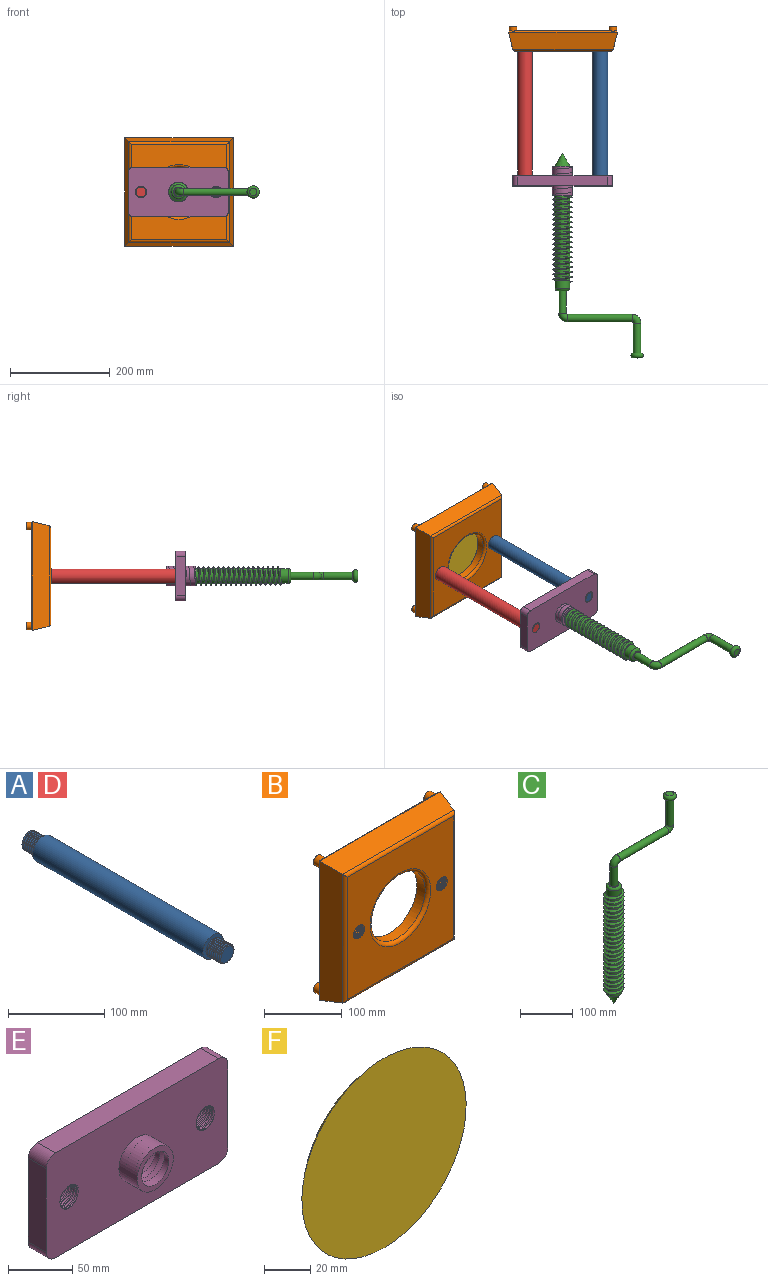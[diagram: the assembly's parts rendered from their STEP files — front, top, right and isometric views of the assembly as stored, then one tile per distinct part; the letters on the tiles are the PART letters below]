
ASSEMBLY  parts=6 mates=5
PART A: 17 faces, bbox 30x293x30 mm
  f0: cylinder r=15mm len=250mm, axis (0,1,0), area 23561.9mm2, adj f1,f2
  f1: plane 30x30mm, normal (0,-1,0), area 392.7mm2, adj f0,f3
  f2: plane 30x30mm, normal (0,1,0), area 392.7mm2, adj f0,f5
  f3: cylinder r=10mm len=20mm, axis (0,1,0), area 531.6mm2, adj f1,f4,f13,f15,f16
  f4: plane 20x20mm, normal (0,-1,0), area 314.2mm2, adj f3,f12
  f5: cylinder r=10mm len=20mm, axis (0,-1,0), area 531.6mm2, adj f2,f6,f8,f10,f11
  f6: plane 20x20mm, normal (0,1,0), area 314.2mm2, adj f5,f7
  f7: cylinder r=10mm len=20mm, axis (0,1,0), area 24.7mm2, adj f6,f9,f10
  f8: plane 1.5x1.3mm, normal (0,0,1), area 1mm2, adj f5,f10,f11
  f9: plane 1.5x1.3mm, normal (0,0,-1), area 1mm2, adj f7,f10,f11
  f10: bspline ~26.09x22.6mm, area 702.4mm2, adj f5,f7,f8,f9,f11
  f11: bspline ~26.09x22.6mm, area 702.4mm2, adj f5,f8,f9,f10
  f12: cylinder r=10mm len=20mm, axis (0,-1,0), area 24.7mm2, adj f4,f14,f15
  f13: plane 1.5x1.3mm, normal (0,0,1), area 1mm2, adj f3,f15,f16
  f14: plane 1.5x1.3mm, normal (0,0,-1), area 1mm2, adj f12,f15,f16
  f15: bspline ~26.09x22.6mm, area 702.4mm2, adj f3,f12,f13,f14,f16
  f16: bspline ~26.09x22.6mm, area 702.4mm2, adj f3,f13,f14,f15
PART B: 45 faces, bbox 219.1x50.6x219.1 mm
  f0: cylinder r=10mm len=20mm, axis (0,-1,0), area 531.6mm2, adj f7,f16,f42,f43,f44
  f1: cylinder r=10mm len=20mm, axis (0,-1,0), area 531.6mm2, adj f7,f16,f39,f40,f41
  f2: plane 214x214mm, normal (0,1,0), area 10968.7mm2, adj f18,f20,f22,f24,f31,f32,f33,f34
  f3: plane 4.31x4.31mm, normal (0,1,0), area 6.6mm2, adj f24,f37,f38
  f4: plane 4.31x4.31mm, normal (0,1,0), area 6.6mm2, adj f22,f36,f38
  f5: plane 4.31x4.31mm, normal (0,1,0), area 6.6mm2, adj f20,f35,f37
  f6: plane 4.31x4.31mm, normal (0,1,0), area 6.6mm2, adj f18,f35,f36
  f7: plane 192.19x192.19mm, normal (0,-1,0), area 26806.2mm2, adj f0,f1,f26,f27,f28,f29,f30
  f8: plane 218.54x33.3mm, normal (0,-0.24,-0.97), area 7216.2mm2, adj f9,f11,f29,f38
  f9: plane 218.54x33.3mm, normal (-0.97,-0.24,0), area 7216.2mm2, adj f8,f10,f27,f37
  f10: plane 218.54x33.3mm, normal (0,-0.24,0.97), area 7216.2mm2, adj f9,f11,f28,f35
  f11: plane 218.54x33.3mm, normal (0.97,-0.24,0), area 7216.2mm2, adj f8,f10,f30,f36
  f12: plane 180x17.66mm, normal (0,0,-1), area 3178.4mm2, adj f13,f15,f16,f34
  f13: plane 180x17.66mm, normal (-1,0,0), area 3178.4mm2, adj f12,f14,f16,f32
  f14: plane 180x17.66mm, normal (0,0,1), area 3178.4mm2, adj f13,f15,f16,f31
  f15: plane 180x17.66mm, normal (1,0,0), area 3178.4mm2, adj f12,f14,f16,f33
  f16: plane 180.6x180.6mm, normal (0,1,0), area 23873.1mm2, adj f0,f1,f12,f13,f14,f15,f17,f40
  f17: cylinder r=50mm len=100mm, axis (0,-1,0), area 4712.4mm2, adj f16,f26
  f18: cylinder r=7.5mm len=15mm, axis (0,-1,0), area 475.9mm2, adj f2,f6,f19,f35,f36
  f19: plane 15x15mm, normal (0,1,0), area 176.7mm2, adj f18
  f20: cylinder r=7.5mm len=15mm, axis (0,-1,0), area 475.9mm2, adj f2,f5,f21,f35,f37
  f21: plane 15x15mm, normal (0,1,0), area 176.7mm2, adj f20
  f22: cylinder r=7.5mm len=15mm, axis (0,-1,0), area 475.9mm2, adj f2,f4,f23,f36,f38
  f23: plane 15x15mm, normal (0,1,0), area 176.7mm2, adj f22
  f24: cylinder r=7.5mm len=15mm, axis (0,-1,0), area 475.9mm2, adj f2,f3,f25,f37,f38
  f25: plane 15x15mm, normal (0,1,0), area 176.7mm2, adj f24
  f26: torus R=55mm, axis (0,-1,0), area 2557.1mm2, adj f7,f17
  f27: cylinder r=5mm len=201.89mm, axis (0,0,1), area 1311.9mm2, adj f7,f9,f28,f29
  f28: cylinder r=5mm len=201.89mm, axis (-1,0,0), area 1311.9mm2, adj f7,f10,f27,f30
  f29: cylinder r=5mm len=201.89mm, axis (-1,0,0), area 1311.9mm2, adj f7,f8,f27,f30
  f30: cylinder r=5mm len=201.89mm, axis (0,0,1), area 1311.9mm2, adj f7,f11,f28,f29
  f31: plane 184.68x2.34mm, normal (0,0.71,0.71), area 604mm2, adj f2,f14,f32,f33
  f32: plane 184.68x2.34mm, normal (-0.71,0.71,0), area 604mm2, adj f2,f13,f31,f34
  f33: plane 184.68x2.34mm, normal (0.71,0.71,0), area 604mm2, adj f2,f15,f31,f34
  f34: plane 184.68x2.34mm, normal (0,0.71,-0.71), area 604mm2, adj f2,f12,f32,f33
  f35: plane 218.54x2.91mm, normal (0,0.62,0.79), area 792.7mm2, adj f2,f5,f6,f10,f18,f20,f36,f37
  f36: plane 218.54x2.91mm, normal (0.79,0.62,0), area 792.7mm2, adj f2,f4,f6,f11,f18,f22,f35,f38
  f37: plane 218.54x2.91mm, normal (-0.79,0.62,0), area 792.7mm2, adj f2,f3,f5,f9,f20,f24,f35,f38
  f38: plane 218.54x2.91mm, normal (0,0.62,-0.79), area 792.7mm2, adj f2,f3,f4,f8,f22,f24,f36,f37
  f39: plane 1.5x1.3mm, normal (0,0,-1), area 1mm2, adj f1,f40,f41
  f40: bspline ~26.09x22.6mm, area 689mm2, adj f1,f16,f39,f41
  f41: bspline ~26.09x22.6mm, area 663mm2, adj f1,f16,f39,f40
  f42: plane 1.5x1.3mm, normal (0,0,-1), area 1mm2, adj f0,f43,f44
  f43: bspline ~26.09x22.6mm, area 689mm2, adj f0,f16,f42,f44
  f44: bspline ~26.09x22.6mm, area 663mm2, adj f0,f16,f42,f43
PART C: 19 faces, bbox 182.9x38.7x410 mm
  f0: cylinder r=7.5mm len=45mm, axis (0,0,1), area 2120.6mm2, adj f1,f8
  f1: torus R=10mm, axis (0,1,0), area 740.2mm2, adj f0,f2
  f2: cylinder r=7.5mm len=130mm, axis (1,0,0), area 6126.1mm2, adj f1,f3
  f3: torus R=10mm, axis (0,-1,0), area 740.2mm2, adj f2,f4
  f4: cylinder r=7.5mm len=60mm, axis (0,0,1), area 2827.4mm2, adj f3,f6
  f5: plane 15x15mm, normal (0,0,1), area 176.7mm2, adj f6
  f6: torus R=7.5mm, axis (0,0,1), area 1054.4mm2, adj f4,f5
  f7: cylinder r=14.69mm len=29.39mm, axis (0,0,-1), area 1384.8mm2, adj f17,f18
  f8: plane 19.39x19.39mm, normal (0,0,1), area 118.5mm2, adj f0,f18
  f9: plane 1x1mm, normal (0,0,-1), area 0.8mm2, adj f11
  f10: plane 5x4.33mm, normal (0,1,0), area 10.8mm2, adj f12,f13,f15
  f11: cone r=0.5mm half-angle=30.1deg, axis (0,0,1), area 1407.3mm2, adj f9,f16
  f12: bspline ~232.5x38.66mm, area 12404.9mm2, adj f10,f13,f14,f16
  f13: bspline ~232.5x38.66mm, area 12404.9mm2, adj f10,f12,f14,f15,f16
  f14: plane 5x4.33mm, normal (0,-1,0), area 10.8mm2, adj f12,f13,f16
  f15: cylinder r=15mm len=30mm, axis (0,0,1), area 117.8mm2, adj f10,f13,f17
  f16: cylinder r=15mm len=230mm, axis (0,0,1), area 11782.1mm2, adj f11,f12,f13,f14,f17
  f17: plane 30x30mm, normal (0,0,1), area 28.6mm2, adj f7,f15,f16
  f18: torus R=9.69mm, axis (0,0,1), area 635.4mm2, adj f7,f8
PART D: same geometry as A
PART E: 26 faces, bbox 200.6x64.3x100.6 mm
  f0: cylinder r=10mm len=20mm, axis (0,1,0), area 531.6mm2, adj f11,f12,f17,f18,f19
  f1: plane 180x20mm, normal (0,0,1), area 3600mm2, adj f2,f10,f11,f12
  f2: cylinder r=10mm len=20mm, axis (0,1,0), area 314.2mm2, adj f1,f3,f11,f12
  f3: plane 80x20mm, normal (-1,0,0), area 1600mm2, adj f2,f4,f11,f12
  f4: cylinder r=10mm len=20mm, axis (0,1,0), area 314.2mm2, adj f3,f5,f11,f12
  f5: plane 180x20mm, normal (0,0,-1), area 3600mm2, adj f4,f6,f11,f12
  f6: cylinder r=10mm len=20mm, axis (0,1,0), area 314.2mm2, adj f5,f7,f11,f12
  f7: plane 80x20mm, normal (1,0,0), area 1600mm2, adj f6,f10,f11,f12
  f8: cylinder r=10mm len=20mm, axis (0,1,0), area 531.6mm2, adj f11,f12,f20,f21,f22
  f9: cylinder r=15mm len=60mm, axis (0,1,0), area 2982mm2, adj f14,f16,f23,f24,f25
  f10: cylinder r=10mm len=20mm, axis (0,1,0), area 314.2mm2, adj f1,f7,f11,f12
  f11: plane 200.6x100.6mm, normal (0,-1,0), area 17984.7mm2, adj f0,f1,f2,f3,f4,f5,f6,f7
  f12: plane 200x100mm, normal (0,1,0), area 18029.2mm2, adj f0,f1,f2,f3,f4,f5,f6,f7
  f13: cylinder r=20mm len=40mm, axis (0,-1,0), area 2513.3mm2, adj f12,f14
  f14: plane 40x40mm, normal (0,1,0), area 437.9mm2, adj f9,f13,f24,f25
  f15: cylinder r=20mm len=40mm, axis (0,1,0), area 2513.3mm2, adj f11,f16
  f16: plane 40x40mm, normal (0,-1,0), area 549.8mm2, adj f9,f15
  f17: plane 1.5x1.3mm, normal (0,0,-1), area 1mm2, adj f0,f18,f19
  f18: bspline ~26.09x22.6mm, area 689mm2, adj f0,f11,f17,f19
  f19: bspline ~26.09x22.6mm, area 663mm2, adj f0,f11,f17,f18
  f20: plane 1.5x1.3mm, normal (0,0,-1), area 1mm2, adj f8,f21,f22
  f21: bspline ~26.09x22.6mm, area 689mm2, adj f8,f11,f20,f22
  f22: bspline ~26.09x22.6mm, area 663mm2, adj f8,f11,f20,f21
  f23: plane 5x4.33mm, normal (0,0,1), area 10.8mm2, adj f9,f24,f25
  f24: bspline ~62.5x38.66mm, area 3168.7mm2, adj f9,f14,f23,f25
  f25: bspline ~61.25x38.66mm, area 3056.5mm2, adj f9,f14,f23,f24
PART F: 2 faces, bbox 100x25.2x100 mm
  f0: plane 100x100mm, normal (0,-1,0), area 7854mm2, adj f1
  f1: torus R=9.48mm, axis (0,-1,0), area 8870.3mm2, adj f0
PLACE A t=(783.13,328.29,-55.86)mm
PLACE B t=(708.13,493.29,-55.86)mm fixed
PLACE C rot(axis=(1,0,0),90deg) t=(706.83,132.54,-55.86)mm
PLACE D t=(631.83,327.54,-55.86)mm
PLACE E t=(706.83,192.54,-55.86)mm
PLACE F t=(708.13,493.29,-55.88)mm
MATE planar D.f0 <-> E.f8  axis (0,-1,0) through (631.83,202.54,-55.86)mm
MATE planar B.f1 <-> A.f3  axis (0,-1,0) through (783.13,453.29,-55.86)mm
MATE planar F.f1 <-> B.f16  axis (0,-1,0) through (708.13,473.29,-55.88)mm
MATE planar B.f42 <-> D.f8  axis (0,0,1) through (643.13,453.29,-55.86)mm
MATE planar C.f15 <-> E.f13  axis (0,-1,0) through (706.83,222.54,-55.86)mm
